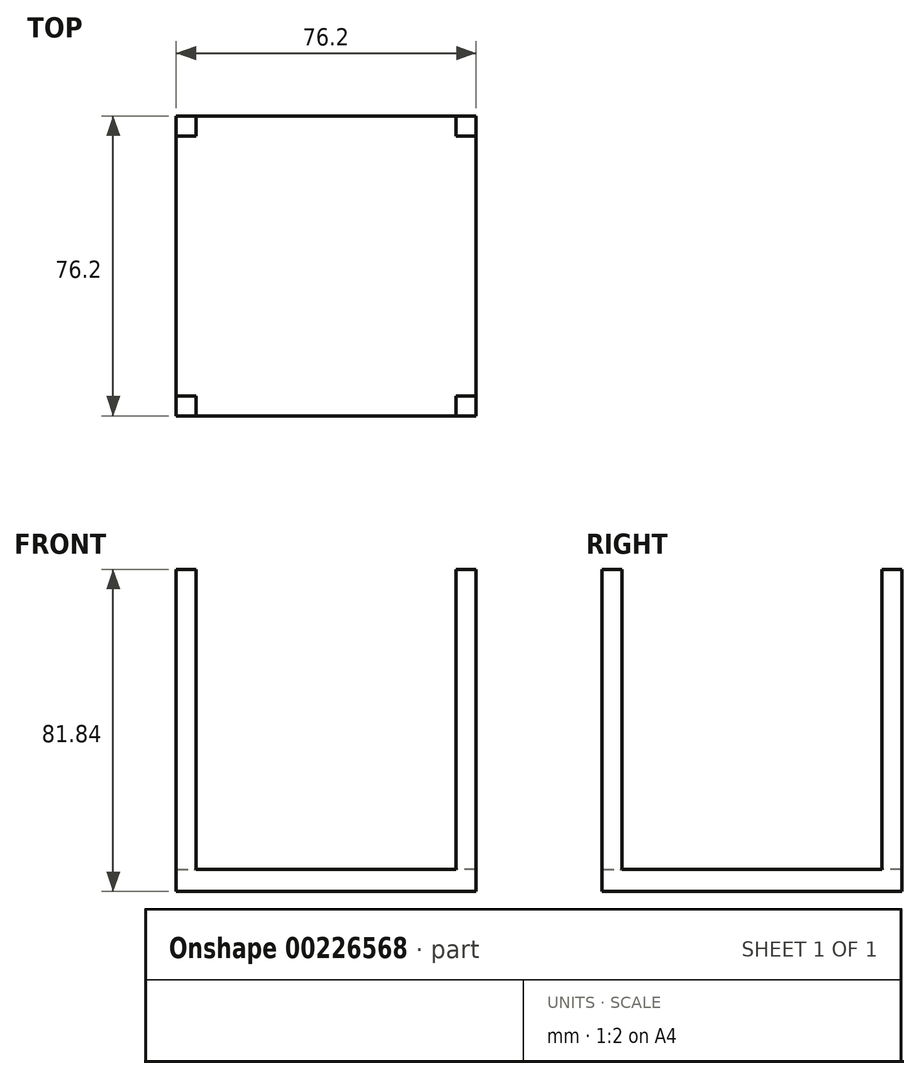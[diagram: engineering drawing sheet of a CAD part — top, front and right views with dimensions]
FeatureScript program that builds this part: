
annotation { "Feature Type Name" : "Feature", "Feature Type Description" : "" }
export const myFeature = defineFeature(function(context is Context, id is Id, definition is map)
    precondition{}
    {
        {
            var Q0;
            Q0=qCreatedBy(makeId("Top.planeOp"),FACE);
            var sketch = newSketch(context, id + "F0", { "sketchPlane" : qUnion([Q0])});
            skLineSegment(sketch, "E0.top", {"start": v(-37.8, 30.6) * mm, "end": v(38.4, 30.6) * mm});
            skLineSegment(sketch, "E0.left", {"start": v(-37.8, -45.6) * mm, "end": v(-37.8, 30.6) * mm});
            skLineSegment(sketch, "E0.right", {"start": v(38.4, -45.6) * mm, "end": v(38.4, 30.6) * mm});
            skLineSegment(sketch, "E1", {"start": v(-37.8, -45.6) * mm, "end": v(38.4, -45.6) * mm});
            skSolve(sketch);
        }
        {
            var Q0;
            Q0 = qSketchRegion(id + "F0", true);
            extrude(context, id + "F1", {"entities" : qUnion([Q0]), "depth" : 5.64 * mm});
        }
        {
            var Q0;
            Q0=makeQuery(id+"F1.opExtrude","CAP_FACE",FACE,{"disambiguationData":[OSD([sQuery(id+"F0.wireOp",EDGE,"E0.top"),sQuery(id+"F0.wireOp",EDGE,"E0.left"),sQuery(id+"F0.wireOp",EDGE,"E0.right"),sQuery(id+"F0.wireOp",EDGE,"E1")])],"isStart":false});
            var sketch = newSketch(context, id + "F2", { "sketchPlane" : qUnion([Q0])});
            skLineSegment(sketch, "E2.bottom", {"start": v(-37.8, 30.6) * mm, "end": v(-32.73, 30.6) * mm});
            skLineSegment(sketch, "E2.top", {"start": v(-37.8, 25.52) * mm, "end": v(-32.73, 25.52) * mm});
            skLineSegment(sketch, "E2.left", {"start": v(-37.8, 30.6) * mm, "end": v(-37.8, 25.52) * mm});
            skLineSegment(sketch, "E2.right", {"start": v(-32.73, 30.6) * mm, "end": v(-32.73, 25.52) * mm});
            skLineSegment(sketch, "E3.bottom", {"start": v(38.4, 30.6) * mm, "end": v(33.31, 30.6) * mm});
            skLineSegment(sketch, "E3.top", {"start": v(38.4, 25.52) * mm, "end": v(33.31, 25.52) * mm});
            skLineSegment(sketch, "E3.left", {"start": v(38.4, 30.6) * mm, "end": v(38.4, 25.52) * mm});
            skLineSegment(sketch, "E3.right", {"start": v(33.31, 30.6) * mm, "end": v(33.31, 25.52) * mm});
            skLineSegment(sketch, "E4.bottom", {"start": v(-37.8, -45.6) * mm, "end": v(-32.73, -45.6) * mm});
            skLineSegment(sketch, "E4.top", {"start": v(-37.8, -40.52) * mm, "end": v(-32.73, -40.52) * mm});
            skLineSegment(sketch, "E4.left", {"start": v(-37.8, -45.6) * mm, "end": v(-37.8, -40.52) * mm});
            skLineSegment(sketch, "E4.right", {"start": v(-32.73, -45.6) * mm, "end": v(-32.73, -40.52) * mm});
            skLineSegment(sketch, "E5.bottom", {"start": v(38.4, -45.6) * mm, "end": v(33.31, -45.6) * mm});
            skLineSegment(sketch, "E5.top", {"start": v(38.4, -40.52) * mm, "end": v(33.31, -40.52) * mm});
            skLineSegment(sketch, "E5.left", {"start": v(38.4, -45.6) * mm, "end": v(38.4, -40.52) * mm});
            skLineSegment(sketch, "E5.right", {"start": v(33.31, -45.6) * mm, "end": v(33.31, -40.52) * mm});
            skSolve(sketch);
        }
        {
            var Q0;
            Q0 = qSketchRegion(id + "F2", true);
            extrude(context, id + "F3", {"entities" : qUnion([Q0]), "operationType" : NewBodyOperationType.ADD, "depth" : 76.2 * mm});
        }
    });
